# Revit family: Gira_543700
name_source: partatom
category: Elektroinstallationen
revit_build: Autodesk Revit 2017 (Build: 20160225_1515(x64)
units: mm (PartAtom-declared; Revit-internal decimal feet)

## family parameters
Basisbauteil = Fläche
Beim Laden mit Abzugskörper schneiden = Nein
Bemaßung runder Anschluss = Durchmesser verwenden
Beschriftungsausrichtung beibehalten = Nein
Gemeinsam genutzt = Nein
Raumberechnungspunkt = Nein
Teiletyp = Normal

## types (1)
- Funk Jal.aktor 1f REG Gira eNet
    Andere Bussysteme = eNet
    Anzahl der Eingänge = 1
    BIM = https://media.stage.bim.site X1 REG KNX.rfa
    BIMSITE_PRODUCT_ID = 19f2b6595787a346dbc975ec627ee395b6337b03
    Beschreibung = eNet Funk Jalousieaktor 1fach  REG Merkmale: Mit eNet Server einstellbar::  Vollverschlüsselte Funkübertragung (AES-CCM) ab eNet Server Software Version 2.0.  Bediensperren.  Update der Gerätesoftware.  Der eNet Funk Jalousieaktor empfängt über eine Datenleitung vom eNet Funk Empfangsmodul oder eNet Server Telegramme zur Steuerung elektrisch betriebener Behänge, wie z. B. Jalousien, Rollläden oder Markisen.  Positionierung von Jalousie und Lamelle über Szenenaufruf.  Positionen für Sonnenschutz und Dämmerung speicherbar.  Schwellwertszenen für Sonnenschutz, Dämmerung und Windalarm.  Statusrückmeldung an eNet Funksender.  Behanglaufzeit speicherbar.  Lamellenumsteuerzeit speicherbar. Mit eNet Server einstellbar::  Umsteuerzeit bei Richtungswechsel.  Laufrichtung invertierbar (z. B. für Dachfenster).  Position bei Sonnenschutz, Dämmerung, Aussperrschutz und Windalarm.  Hinweise :  Zum Betrieb dieses Reiheneinbaugeräts wird ein eNet Funk Empfangsmodul oder ein eNet Server benötigt.
    Breite in Teilungseinheiten = 2
    Bussystem Funkbus = Ja
    Bussystem KNX = Nein
    Bussystem KNX-Funk = Nein
    Bussystem LON = Nein
    Bussystem Powernet = Nein
    Datenblatt = https://media.stage.bim.site
    Datenblatt 1 = https://media.stage.bim.site
    Funktion Schalten = Nein
    GTIN = 4010337774297
    HAN = 543700
    HeinzeBIM = https://www.heinze.de
    Hersteller = Gira
    Kosten = 0 $
    Max. Anzahl der Jalousieausgänge = 1
    Max. Schaltleistung [Voltampere] = 1000
    Mit Busankopplung = Nein
    Mit LED-Anzeige = Nein
    Montageart = REG
    Produktseite = https://media.stage.bim.site
    Schutzart (IP) = IP20
    Stromart = AC
    Typname = Funk Jal.aktor 1f REG Gira eNet
    URL = https://www.gira.de
    Vor Ort-/Handbedienung = Nein
    Vorgabe-Ansicht = 1219 mm

## geometry (parser evidence)
native form markers: Sweep x2
no freeform markers — native parametric forms only
